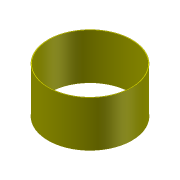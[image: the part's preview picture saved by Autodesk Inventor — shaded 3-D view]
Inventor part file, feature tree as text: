
AUTODESK INVENTOR PART (.ipt)
format: ipt  version: 2012 (Build 160160000, 160)  size: 80,896 bytes
history: native  units: in
note: dims shown in document units (in); Inventor stores cm internally (conversion verified against a paired STEP export)
features: extrude x1, sketch x1
ambient origin geometry x8: Origin, YZ Plane, XZ Plane, XY Plane, X Axis, Y Axis, Z Axis, Center Point
bodies: Solid1 (feature_tree)
feature tree (2):
  extrude  "Extrusion1"  Depth=55.0in
  sketch  "Sketch2"  dims[d0=54.0in d1=55.0in d2=30.0in d3=0.0in]
